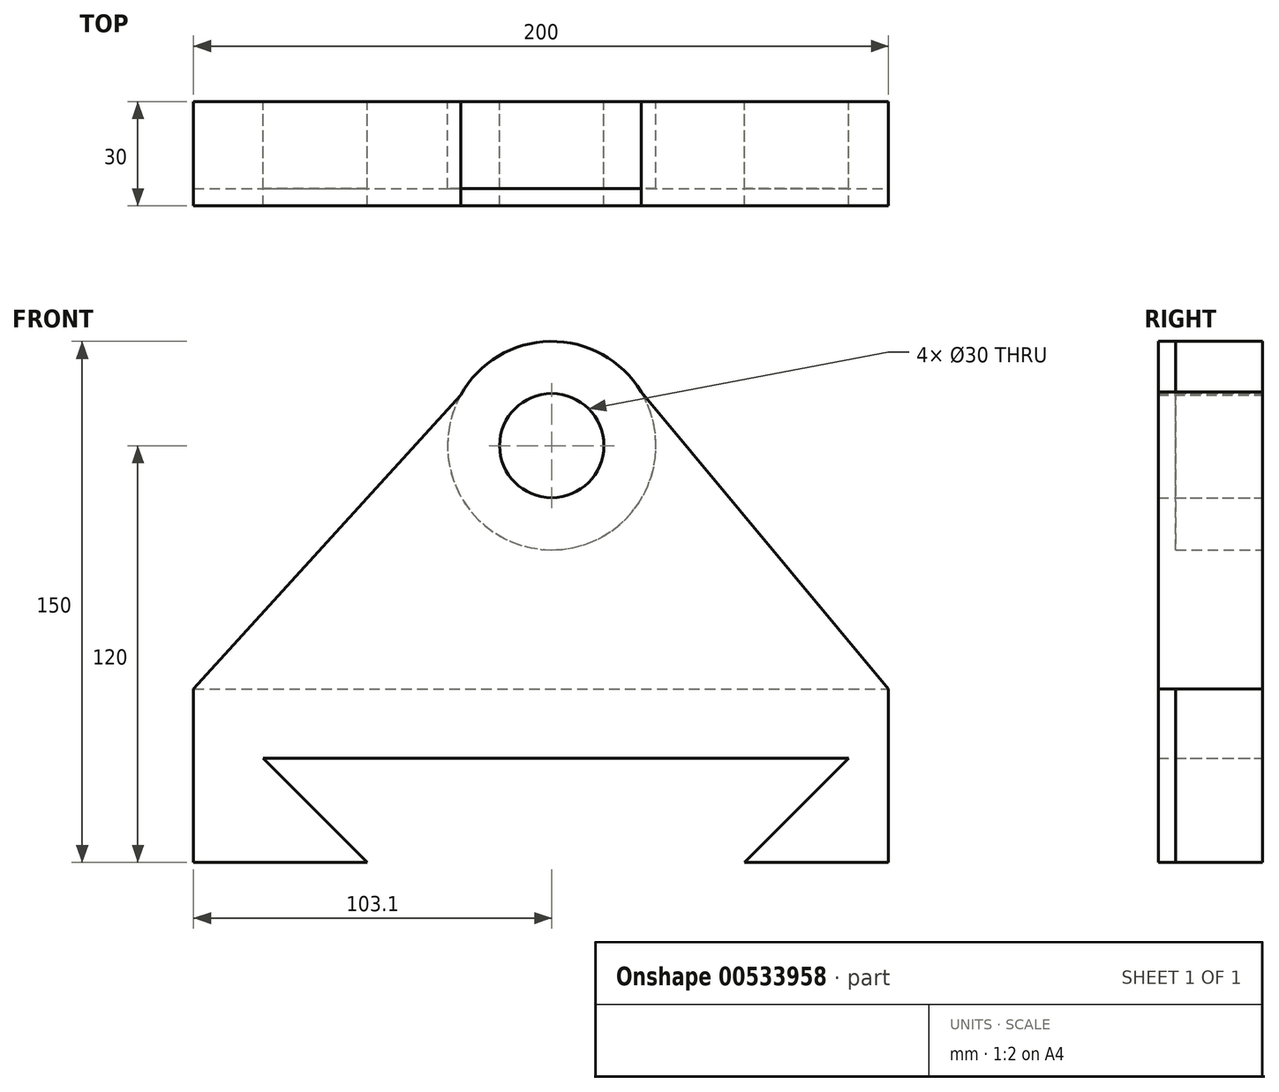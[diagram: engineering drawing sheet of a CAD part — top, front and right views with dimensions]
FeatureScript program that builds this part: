
annotation { "Feature Type Name" : "Feature", "Feature Type Description" : "" }
export const myFeature = defineFeature(function(context is Context, id is Id, definition is map)
    precondition{}
    {
        {
            var Q0;
            Q0=qCreatedBy(makeId("Front.planeOp"),FACE);
            var sketch = newSketch(context, id + "F0", { "sketchPlane" : qUnion([Q0])});
            skLineSegment(sketch, "E0", {"start": v(-103.1, -50) * mm, "end": v(-53.1, -50) * mm});
            skLineSegment(sketch, "E1", {"start": v(-53.1, -50) * mm, "end": v(-83.1, -20) * mm});
            skLineSegment(sketch, "E2", {"start": v(-103.1, -50) * mm, "end": v(-103.1, 0) * mm});
            skCircle(sketch, "E3", {"center": v(0, 70) * mm, "radius": 30 * mm});
            skCircle(sketch, "E4", {"center": v(0, 70) * mm, "radius": 15 * mm});
            skLineSegment(sketch, "E5", {"start": v(55.48, -50) * mm, "end": v(96.9, -50) * mm});
            skPoint(sketch, "E6.end.orphan", {"position": v(49.8, -20) * mm});
            skLineSegment(sketch, "E7", {"start": v(-83.1, -20) * mm, "end": v(85.48, -20) * mm});
            skLineSegment(sketch, "E8", {"start": v(85.48, -20) * mm, "end": v(55.48, -50) * mm});
            skPoint(sketch, "E9.orphan", {"position": v(35.69, -50) * mm});
            skLineSegment(sketch, "E10", {"start": v(96.9, -50) * mm, "end": v(96.9, 0) * mm});
            skLineSegment(sketch, "E11", {"start": v(-103.1, 0) * mm, "end": v(96.9, 0) * mm});
            skLineSegment(sketch, "E12", {"start": v(-103.1, 0) * mm, "end": v(-26.22, 84.59) * mm});
            skLineSegment(sketch, "E13", {"start": v(96.9, 0) * mm, "end": v(25.7, 85.48) * mm});
            skSolve(sketch);
        }
        {
            var Q0;
            Q0=makeQuery(id+"F0.imprint","IMPRINT",FACE,{"disambiguationData":[TD([[makeQuery(id+"F0.imprint","IMPRINT",EDGE,{"derivedFrom":sQuery(id+"F0.wireOp",EDGE,"E0")}),1.0]])]});
            var Q1;
            Q1=makeQuery(id+"F0.imprint","IMPRINT",FACE,{"disambiguationData":[TD([[makeQuery(id+"F0.imprint","IMPRINT",EDGE,{"derivedFrom":sQuery(id+"F0.wireOp",EDGE,"E4")}),-1.0]])]});
            extrude(context, id + "F1", {"entities" : qUnion([Q0, Q1]), "depth" : 25 * mm, "offsetDistance" : 25 * mm});
        }
        {
            var Q0;
            Q0 = qSketchRegion(id + "F0", true);
            extrude(context, id + "F2", {"entities" : qUnion([Q0]), "depth" : 30 * mm, "offsetDistance" : 25 * mm});
        }
    });
